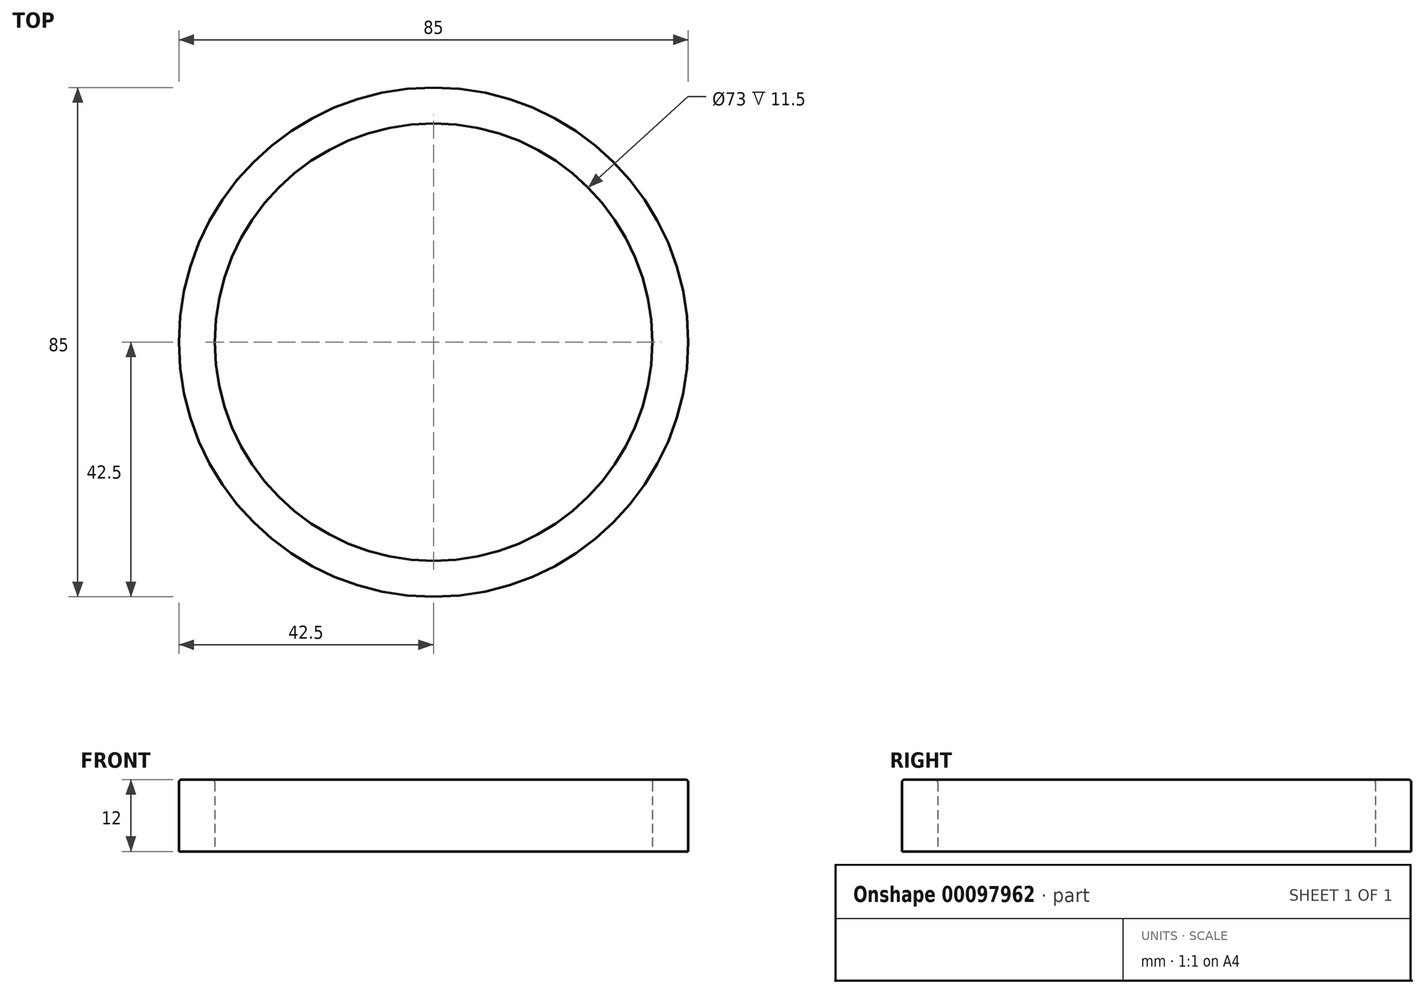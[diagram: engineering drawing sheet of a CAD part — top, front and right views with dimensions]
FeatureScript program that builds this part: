
annotation { "Feature Type Name" : "Feature", "Feature Type Description" : "" }
export const myFeature = defineFeature(function(context is Context, id is Id, definition is map)
    precondition{}
    {
        {
            var Q0;
            Q0=qCreatedBy(makeId("Top.planeOp"),FACE);
            var sketch = newSketch(context, id + "F0", { "sketchPlane" : qUnion([Q0])});
            skCircle(sketch, "E0", {"center": v(0, 0) * mm, "radius": 42.5 * mm});
            skCircle(sketch, "E1", {"center": v(0, 0) * mm, "radius": 36.5 * mm});
            skSolve(sketch);
        }
        {
            var Q0;
            Q0 = qSketchRegion(id + "F0", true);
            extrude(context, id + "F1", {"entities" : qUnion([Q0]), "depth" : 12 * mm});
        }
        {
            var Q0;
            Q0=makeQuery(id+"F1.opExtrude","CAP_FACE",FACE,{"disambiguationData":[OSD([sQuery(id+"F0.wireOp",EDGE,"E0"),sQuery(id+"F0.wireOp",EDGE,"E1")])],"isStart":false});
            fillet(context, id + "F2", {"entities" : qUnion([Q0]), "radius" : 0.5 * mm, "tangentPropagation" : true, "allowEdgeOverflow" : false});
        }
    });
